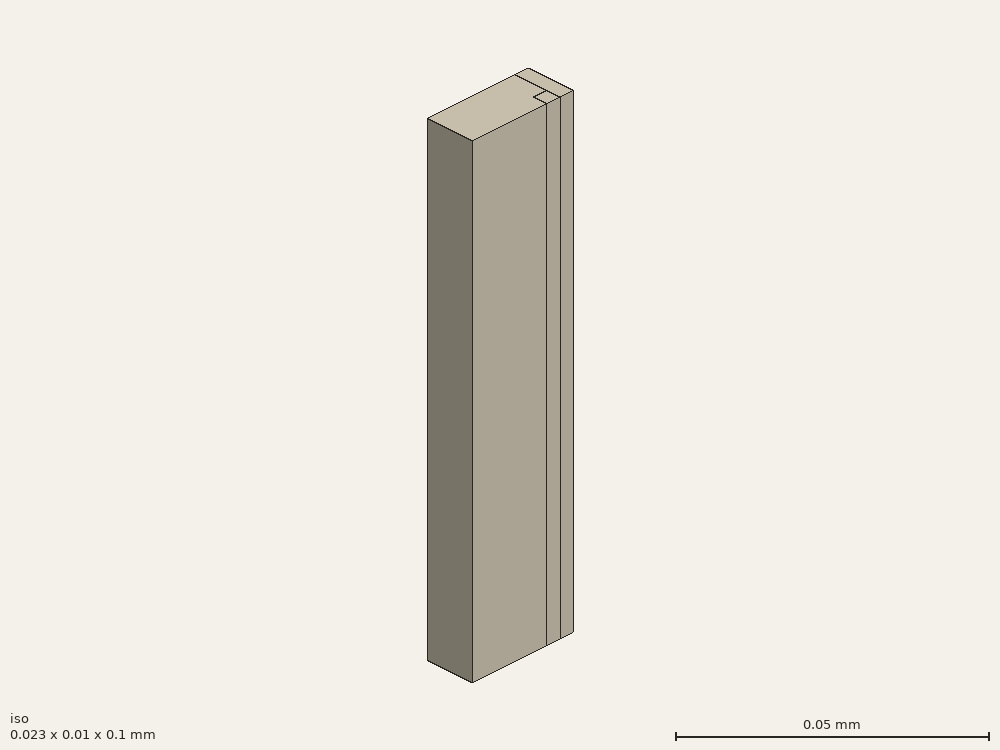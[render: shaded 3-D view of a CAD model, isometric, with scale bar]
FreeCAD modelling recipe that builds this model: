
FCSTD DOCUMENT  (FreeCAD 0.21R33694 (Git))
Label: straight-asymmetric
License: All rights reserved
LicenseURL: http://en.wikipedia.org/wiki/All_rights_reserved
objects: Part::Part2DObjectPython×7, App::FeaturePython×4, Part::Extrusion×3, Part::FeaturePython×1
note: 11 computed .brp shape members not serialized (recipe doc carries the construction recipe); baked Part::Feature solids carry a one-line shape summary decoded from their .brp

FEATURE [Part::Part2DObjectPython] Rectangle001  label="_Pport1"  # Draft 2D object (typed FeaturePython)
  Area = 0.000232258
  ChamferSize = 0
  Columns = 1
  FilletRadius = 0
  Height = 0.01016
  Length = 0.02286
  MakeFace = true
  Placement = pos=(-0.01143,-0.00508,0.1) rot=(0,0,1;0rad)
  Rows = 1
FEATURE [Part::Part2DObjectPython] Line  label="_Pv1"  # Draft 2D object (typed FeaturePython)
  Area = 0
  ChamferSize = 0
  Closed = false
  End = (-1.8e-15,0.00508,0.1)
  FilletRadius = 0
  Length = 0.01016
  MakeFace = true
  Placement = pos=(0,-0.00508,0.1) rot=(0,0,1;0rad)
  Points = (2) [(0,0,0),(-1.77605e-15,0.01016,0)]
  Start = (0,-0.00508,0.1)
  Subdivisions = 0
FEATURE [Part::Part2DObjectPython] Rectangle002  label="_Pport2"  # Draft 2D object (typed FeaturePython)
  Area = 0.000232258
  ChamferSize = 0
  Columns = 1
  FilletRadius = 0
  Height = 0.01016
  Length = 0.02286
  MakeFace = true
  Placement = pos=(-0.01143,-0.00508,0) rot=(0,0,1;0rad)
  Rows = 1
FEATURE [Part::Part2DObjectPython] Line001  label="_Pv2"  # Draft 2D object (typed FeaturePython)
  Area = 0
  ChamferSize = 0
  Closed = false
  End = (0,0.00508,0)
  FilletRadius = 0
  Length = 0.01016
  MakeFace = true
  Placement = pos=(0,-0.00508,0) rot=(0,0,1;0rad)
  Points = (2) [(0,0,0),(3.1106e-19,0.01016,0)]
  Start = (0,-0.00508,0)
  Subdivisions = 0
FEATURE [App::FeaturePython] Text  label="_Sinput(PV){port1}"  # WARN: FeaturePython — macro-defined, semantics opaque (R4)
  Placement = pos=(0.0413747,-0.017509,0) rot=(0,0,1;0rad)
  Text = .
FEATURE [App::FeaturePython] Text001  label="_Soutput(PV){port2}"  # WARN: FeaturePython — macro-defined, semantics opaque (R4)
  Placement = pos=(0.0413747,-0.017509,0) rot=(0,0,1;0rad)
  Text = .
FEATURE [App::FeaturePython] Text002  label="_Linput(1,voltage){v1}"  # WARN: FeaturePython — macro-defined, semantics opaque (R4)
  Placement = pos=(0.0413747,-0.017509,0) rot=(0,0,1;0rad)
  Text = .
FEATURE [App::FeaturePython] Text003  label="_Loutput(2,voltage){v2}"  # WARN: FeaturePython — macro-defined, semantics opaque (R4)
  Placement = pos=(0.0413747,-0.017509,0) rot=(0,0,1;0rad)
  Text = .
FEATURE [Part::Part2DObjectPython] Rectangle005  # Draft 2D object (typed FeaturePython)
  Area = 0.000232258
  ChamferSize = 0
  Columns = 1
  FilletRadius = 0
  Height = 0.01016
  Length = 0.02286
  MakeFace = true
  Placement = pos=(-0.01143,-0.00508,0.1) rot=(0,0,1;0rad)
  Rows = 1
FEATURE [Part::Extrusion] Extrude003
  Base = -> Rectangle005
  Dir = (0,0,1)
  DirMode = 2
  FaceMakerClass = Part::FaceMakerBullseye
  LengthFwd = -0.1
  LengthRev = 0
  Solid = false
  Symmetric = false
FEATURE [Part::Part2DObjectPython] Rectangle006  # Draft 2D object (typed FeaturePython)
  Area = 3.048e-05
  ChamferSize = 0
  Columns = 1
  FilletRadius = 0
  Height = 0.01016
  Length = 0.003
  MakeFace = true
  Placement = pos=(0.00843,-0.00508,0.1) rot=(0,0,1;0rad)
  Rows = 1
FEATURE [Part::Part2DObjectPython] Rectangle007  # Draft 2D object (typed FeaturePython)
  Area = 9e-06
  ChamferSize = 0
  Columns = 1
  FilletRadius = 0
  Height = 0.003
  Length = 0.003
  MakeFace = true
  Placement = pos=(0.00543,-0.00508,0.1) rot=(0,0,1;0rad)
  Rows = 1
FEATURE [Part::Extrusion] Extrude
  Base = -> Rectangle006
  Dir = (0,0,1)
  DirMode = 2
  FaceMakerClass = Part::FaceMakerBullseye
  LengthFwd = -0.1
  LengthRev = 0
  Solid = false
  Symmetric = false
FEATURE [Part::Extrusion] Extrude004
  Base = -> Rectangle007
  Dir = (0,0,1)
  DirMode = 2
  FaceMakerClass = Part::FaceMakerBullseye
  LengthFwd = -0.1
  LengthRev = 0
  Solid = false
  Symmetric = false
FEATURE [Part::FeaturePython] BooleanFragments  # WARN: FeaturePython — macro-defined, semantics opaque (R4)
  Mode = 0
  Objects = -> [Extrude003,Extrude,Extrude004]
  Tolerance = 0
